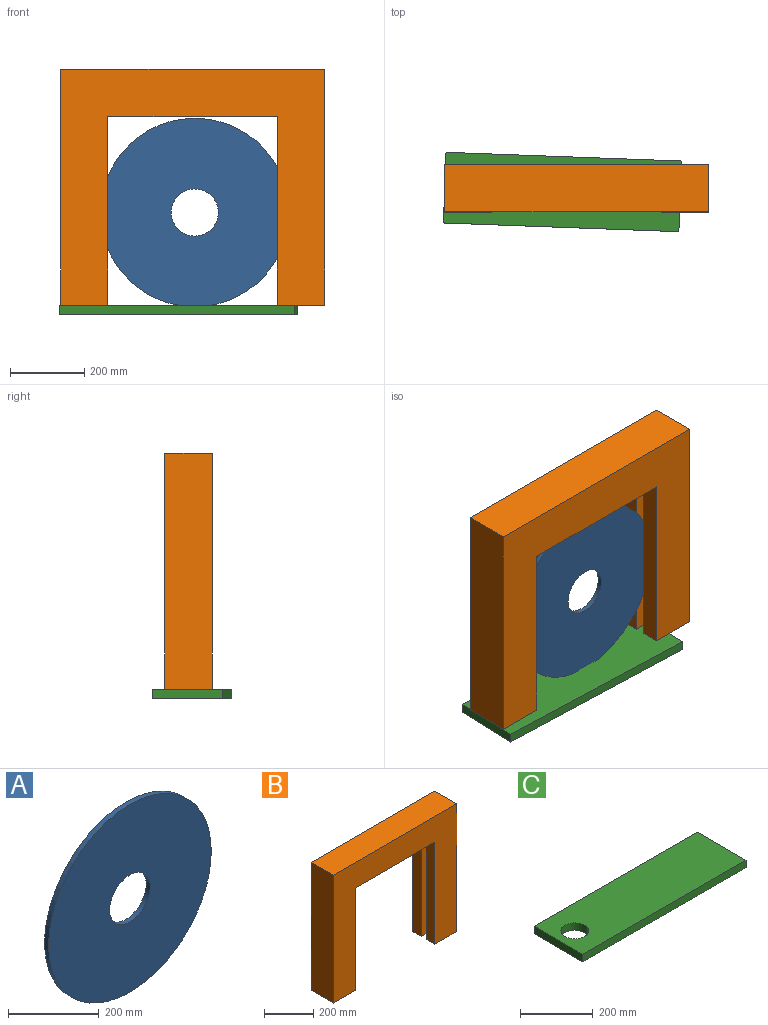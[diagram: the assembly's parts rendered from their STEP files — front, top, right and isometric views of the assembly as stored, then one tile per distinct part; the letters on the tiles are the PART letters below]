
ASSEMBLY  parts=3 mates=3
PART A: 6 faces, bbox 508x12.7x508 mm
  f0: cylinder r=254mm len=508mm, axis (0,1,0), area 20268.3mm2, adj f2,f3,f4
  f1: cylinder r=63.5mm len=127mm, axis (0,1,0), area 5067.1mm2, adj f2,f3
  f2: plane 508x508mm, normal (0,-1,0), area 190015.3mm2, adj f0,f1
  f3: plane 508x508mm, normal (0,1,0), area 190015.3mm2, adj f0,f1
  f4: cylinder r=1.27mm len=127mm, axis (1,0,0), area 1013.4mm2, adj f0,f5
  f5: plane 2.54x2.54mm, normal (1,0,0), area 5.1mm2, adj f4
PART B: 20 faces, bbox 711.2x127x635 mm
  f0: plane 508x50.8mm, normal (1,0,0), area 25806.4mm2, adj f2,f7,f13,f15
  f1: plane 508x50.8mm, normal (-1,0,0), area 25806.4mm2, adj f3,f7,f13,f19
  f2: plane 127x127mm, normal (0,0,-1), area 12133.6mm2, adj f0,f4,f6,f11,f12,f13,f14,f15
  f3: plane 127x127mm, normal (0,0,-1), area 14838.7mm2, adj f1,f8,f9,f12,f13,f17,f18,f19
  f4: cylinder r=31.75mm len=127mm, axis (0,0,-1), area 22016.7mm2, adj f2,f5,f14,f15
  f5: plane 63.5x60.85mm, normal (0,0,-1), area 2705.1mm2, adj f4,f14,f15,f16
  f6: plane 508x50.8mm, normal (1,0,0), area 25806.4mm2, adj f2,f7,f12,f14
  f7: plane 558.8x127mm, normal (0,0,-1), area 60645mm2, adj f0,f1,f6,f8,f12,f13,f14,f15
  f8: plane 508x50.8mm, normal (-1,0,0), area 25806.4mm2, adj f3,f7,f12,f18
  f9: plane 635x127mm, normal (1,0,0), area 80645mm2, adj f3,f10,f12,f13
  f10: plane 711.2x127mm, normal (0,0,1), area 90322.4mm2, adj f9,f11,f12,f13
  f11: plane 635x127mm, normal (-1,0,0), area 80645mm2, adj f2,f10,f12,f13
  f12: plane 711.2x635mm, normal (0,1,0), area 219354.4mm2, adj f2,f3,f6,f7,f8,f9,f10,f11
  f13: plane 711.2x635mm, normal (0,-1,0), area 219354.4mm2, adj f0,f1,f2,f3,f7,f9,f10,f11
  f14: plane 508x50.8mm, normal (0,-1,0), area 23723.7mm2, adj f2,f4,f5,f6,f7,f16
  f15: plane 508x50.8mm, normal (0,1,0), area 23723.7mm2, adj f0,f2,f4,f5,f7,f16
  f16: plane 381x25.4mm, normal (1,0,0), area 9677.4mm2, adj f5,f7,f14,f15
  f17: plane 508x25.4mm, normal (-1,0,0), area 12903.2mm2, adj f3,f7,f18,f19
  f18: plane 508x50.8mm, normal (0,-1,0), area 25806.4mm2, adj f3,f7,f8,f17
  f19: plane 508x50.8mm, normal (0,1,0), area 25806.4mm2, adj f1,f3,f7,f17
PART C: 7 faces, bbox 635x190.5x25.4 mm
  f0: plane 635x25.4mm, normal (0,1,0), area 16129mm2, adj f1,f4,f5,f6
  f1: plane 190.5x25.4mm, normal (-1,0,0), area 4838.7mm2, adj f0,f2,f5,f6
  f2: plane 635x25.4mm, normal (0,-1,0), area 16129mm2, adj f1,f4,f5,f6
  f3: cylinder r=38.1mm len=76.2mm, axis (0,0,-1), area 6080.5mm2, adj f5,f6
  f4: plane 190.5x25.4mm, normal (1,0,0), area 4838.7mm2, adj f0,f2,f5,f6
  f5: plane 635x190.5mm, normal (0,0,1), area 116407.1mm2, adj f0,f1,f2,f3,f4
  f6: plane 635x190.5mm, normal (0,0,-1), area 116407.1mm2, adj f0,f1,f2,f3,f4
PLACE A t=(-8.81,6.75,-13.54)mm
PLACE B t=(-14.55,6.75,-9.03)mm fixed
PLACE C rot(axis=(0,0,-1),2.1deg) t=(-52.83,-2.65,-275.73)mm
MATE cylindrical B.f4 <-> C.f3  axis (0,0,-1) through (-306.65,6.75,-263.03)mm
MATE planar C.f5 <-> B.f2  axis (0,0,1) through (-42.88,-3.02,-263.03)mm
MATE planar A.f0 <-> B.f19  axis (0,-1,0) through (-8.81,-5.95,-13.54)mm
